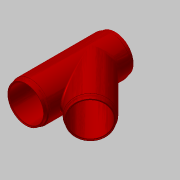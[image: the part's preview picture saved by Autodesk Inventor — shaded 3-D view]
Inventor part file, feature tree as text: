
AUTODESK INVENTOR PART (.ipt)
format: ipt  version: 2017.3 (Build 213257000, 257)  size: 352,768 bytes
history: native  units: in
note: dims shown in document units (in); Inventor stores cm internally (conversion verified against a paired STEP export)
features: extrude x12, sketch x8, fillet x6, chamfer x2, plane x1
ambient origin geometry x8: Origin, YZ Plane, XZ Plane, XY Plane, X Axis, Y Axis, Z Axis, Center Point
bodies: Solid1 (feature_tree)
feature tree (29):
  sketch  "Sketch1"  dims[d0=26.5in d1=29.0in]
  extrude  "Extrusion1"  Depth=29.0in
  plane  "Work Plane1"
  sketch  "Sketch2"  dims[d2=31.0in d3=50.9921in d4=19.4961in d5=0.0in d6=0.0in]
  extrude  "Extrusion2"  Depth=50.9921in TaperAngle=0.0deg
  extrude  "Extrusion3"  Depth=26.5in
  extrude  "Extrusion4"  Depth=31.0in
  extrude  "Extrusion5"  Depth=50.9921in
  extrude  "Extrusion6"  Depth=0.5in
  extrude  "Extrusion7"  TaperAngle=0.0deg  [1 undecoded]
  extrude  "Extrusion8"  Depth=0.5in
  extrude  "Extrusion9"  TaperAngle=0.0deg  [1 undecoded]
  fillet  "Fillet1"  Radius=47.9921in
  fillet  "Fillet2"  Radius=16.4961in
  fillet  "Fillet3"  [1 undecoded]
  fillet  "Fillet4"  Radius=47.9921in
  extrude  "Extrusion10"  TaperAngle=0.0deg  [1 undecoded]
  extrude  "Extrusion11"  Depth=50.9921in
  extrude  "Extrusion12"  TaperAngle=0.0deg  [1 undecoded]
  fillet  "Fillet5"  Radius=50.9921in
  chamfer  "Chamfer3"  [1 undecoded]
  fillet  "Fillet6"  Radius=1.0in
  chamfer  "Chamfer4"  Distance=6.0in
  sketch  "Sketch3"  dims[d7=45.0deg d8=26.5in]
  sketch  "Sketch4"  dims[d9=29.0in d10=31.0in]
  sketch  "Sketch5"  dims[d11=50.9921in d12=0.0in d13=28.0in]
  sketch  "Sketch6"  dims[d14=0.5in d15=0.0in d16=28.0in]
  sketch  "Sketch7"  dims[d17=0.5in d18=0.0in]
  sketch  "Sketch8"  dims[d19=28.0in d20=0.5in d21=0.0in d22=47.9921in d23=16.4961in d24=0.0in d25=0.0in d26=47.9921in d27=0.0in d28=50.9921in d29=0.0in d30=50.9921in d31=0.0in d32=1.0in d33=6.0in d34=1.0in d35=1.0in d39=30.48in d40=1.0in d41=0.0in d42=30.48in d43=1.0in d44=0.0in d45=30.48in d46=1.0in d47=0.0in d48=0.0312in d52=0.74in d53=0.125in d54=45.0deg d55=0.0312in d56=0.0312in d57=0.125in d58=45.0deg]
note: 6 required parameter values undecoded (feature->parameter linkage not recoverable at this tier; creation-order binding heuristic only, values carry confidence <= 0.55)
